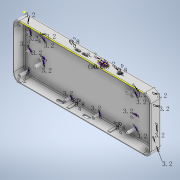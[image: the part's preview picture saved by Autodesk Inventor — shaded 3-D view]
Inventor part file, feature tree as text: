
AUTODESK INVENTOR PART (.ipt)
format: ipt  version: 2022 (Build 260153000, 153)  size: 679,424 bytes
history: native  units: mm
features: sketch x10, extrude x9, fillet x6, hole x3, chamfer x3, revolve x2, other x2, shell x1
ambient origin geometry x8: Origin, YZ Plane, XZ Plane, XY Plane, X Axis, Y Axis, Z Axis, Center Point
bodies: 实体1 (feature_tree)
feature tree (36):
  extrude  "拉伸1"  Depth=1.5mm
  shell  "抽壳1"  Thickness=13.13mm
  fillet  "圆角1"  Radius=1.5mm
  fillet  "圆角2"  Radius=8.0mm
  sketch  "草图2"  dims[d6=8.0mm d7=3.2mm]
  extrude  "拉伸2"  Depth=3.2mm
  hole  "孔2"  [1 undecoded]
  extrude  "拉伸3"  Depth=8.13mm TaperAngle=0.0deg
  hole  "孔3"  [1 undecoded]
  sketch  "草图12"  dims[d20=0.929367mm d21=4.0mm d22=4.0mm d23=2.0mm d24=90.0deg d25=4.0mm d26=0.0mm d27=3.2mm]
  extrude  "拉伸4"  Depth=3.2mm
  extrude  "拉伸5"  Depth=3.2mm
  extrude  "拉伸7"  Depth=3.2mm
  hole  "孔5"  [1 undecoded]
  fillet  "圆角3"  Radius=2.0mm
  extrude  "拉伸8"  Depth=5.7mm
  extrude  "拉伸9"  Depth=5.7mm
  sketch  "草图19"  dims[d38=0.929367mm d39=3.5mm d40=4.0mm d41=2.0mm d42=90.0deg d43=3.5mm d44=0.0mm d47=2.0mm d49=2.0mm d51=13.7mm d52=2.2mm d55=8.23mm d56=3.48mm d57=1.0mm d58=2.0mm d59=2.0mm d60=2.0mm d61=0.0mm d63=1.5mm d64=0.0mm d65=1.5mm d66=0.0mm d67=3.2mm d70=3.2mm d80=3.2mm d81=3.2mm d82=11.13mm d83=0.0mm d84=0.929367mm d85=4.0mm d86=4.0mm d87=2.0mm d88=90.0deg d89=4.0mm d90=0.0mm d91=5.4mm d92=5.5mm d93=3.0mm d94=3.0mm d95=0.0mm d96=3.0mm d97=3.0mm d98=0.0mm d99=3.0mm d100=0.5mm d101=0.0mm d102=3.0mm d103=0.0mm d104=3.0mm d105=0.5mm d106=0.0mm d109=7.1mm d110=3.1mm d111=7.1mm d112=0.0mm d113=3.1mm d114=7.1mm d115=3.1mm d116=0.8mm d117=90.0deg d118=15.0deg d119=15.0deg d120=0.9mm d121=0.3mm d122=45.0deg d123=0.9mm d124=0.3mm d125=45.0deg d126=1.87mm d127=1.9mm d128=0.7mm d129=1.0mm d130=0.3mm d131=45.0deg d132=0.5mm d133=1.0mm d134=3.2mm d135=3.2mm d136=3.2mm d137=3.2mm d146=3.0mm d147=0.8mm d148=3.0mm d149=0.8mm d150=3.0mm d151=0.8mm d152=3.0mm d153=0.8mm d154=1.5mm d155=6.0mm d156=40.0mm d158=4.0mm d159=10.0mm d161=10.0mm d163=5.7mm d164=0.0mm]
  revolve  "旋转3"  [1 undecoded]
  revolve  "旋转4"  [1 undecoded]
  chamfer  "倒角1"  Distance=3.48mm
  chamfer  "倒角2"  Distance=1.0mm
  other  "面圆角1"
  other  "面圆角2"
  fillet  "圆角4"  Radius=2.0mm
  chamfer  "倒角3"  Distance=2.0mm
  fillet  "圆角5"  Radius=2.0mm
  fillet  "圆角6"  [1 undecoded]
  extrude  "拉伸10"  Depth=1.5mm TaperAngle=0.0deg
  sketch  "草图1"  dims[d0=170.0mm d1=65.0mm d2=13.13mm d3=0.0mm d4=1.5mm d5=8.0mm]
  sketch  "草图6"  dims[d8=3.2mm d9=3.2mm]
  sketch  "草图8"  dims[d10=3.2mm d11=8.13mm d12=0.0mm]
  sketch  "草图13"  dims[d28=3.2mm d30=3.2mm]
  sketch  "草图15"  dims[d31=3.2mm d32=3.2mm]
  sketch  "草图16"  dims[d33=3.2mm d34=3.2mm]
  sketch  "草图17"  dims[d35=3.2mm d36=4.78mm d37=0.0mm]
note: 6 required parameter values undecoded (feature->parameter linkage not recoverable at this tier; creation-order binding heuristic only, values carry confidence <= 0.55)